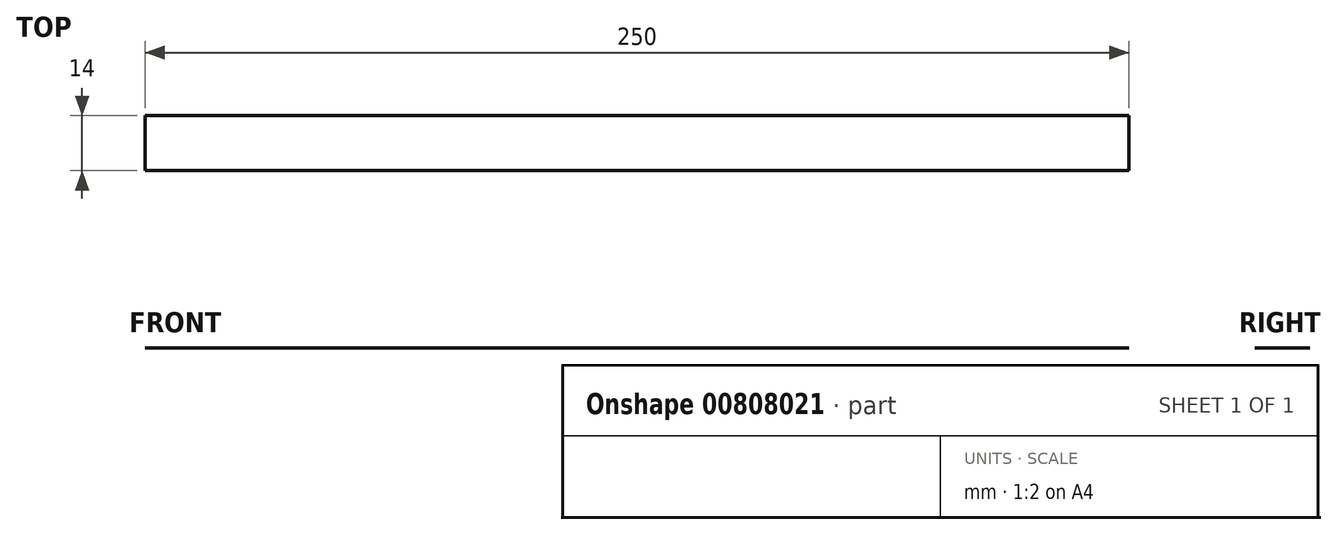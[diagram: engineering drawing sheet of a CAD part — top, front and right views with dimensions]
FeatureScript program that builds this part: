
annotation { "Feature Type Name" : "Feature", "Feature Type Description" : "" }
export const myFeature = defineFeature(function(context is Context, id is Id, definition is map)
    precondition{}
    {
        {
            var Q0;
            Q0=qCreatedBy(makeId("Front.planeOp"),FACE);
            var sketch = newSketch(context, id + "F0", { "sketchPlane" : qUnion([Q0])});
            skLineSegment(sketch, "E0", {"start": v(-78.51, 47.05) * mm, "end": v(-78.51, 297.05) * mm});
            skLineSegment(sketch, "E1", {"start": v(-78.51, 47.05) * mm, "end": v(-78.51, -202.95) * mm});
            skLineSegment(sketch, "E2", {"start": v(-78.51, 47.05) * mm, "end": v(171.49, 47.05) * mm});
            skLineSegment(sketch, "E3", {"start": v(-78.51, 47.05) * mm, "end": v(-328.51, 47.05) * mm});
            skSolve(sketch);
        }
        {
            var Q0;
            Q0=sQuery(id+"F0.wireOp",EDGE,"E3");
            extrude(context, id + "F1", {"bodyType" : ToolBodyType.SURFACE, "surfaceEntities" : qUnion([Q0]), "depth" : 14 * mm, "offsetDistance" : 25 * mm});
        }
    });
